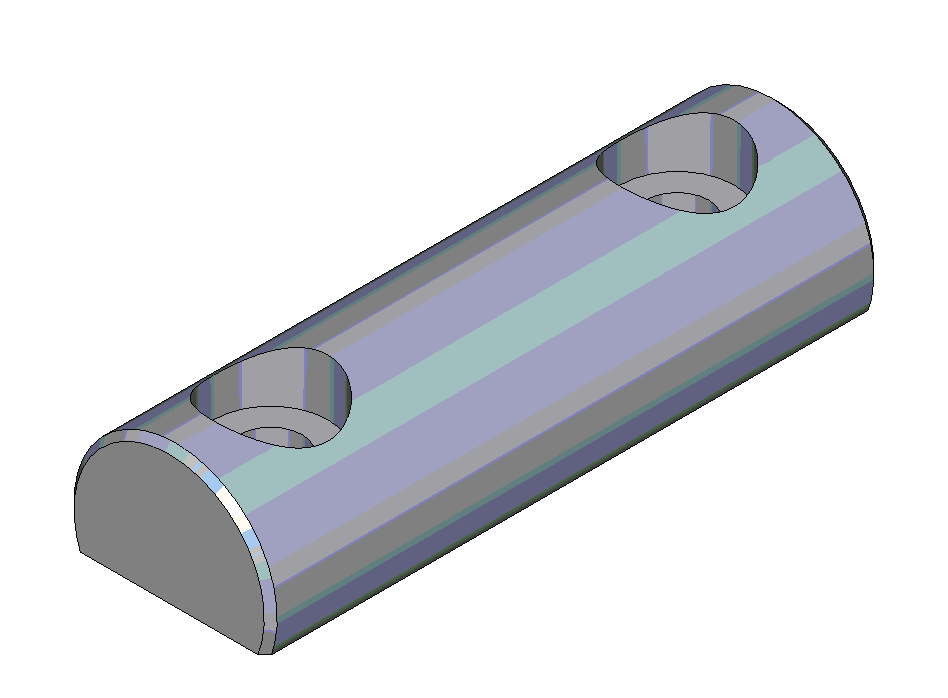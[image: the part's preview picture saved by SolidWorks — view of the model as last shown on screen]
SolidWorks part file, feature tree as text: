
SOLIDWORKS PART (.sldprt)
format: sldprt  version: not decoded by parser v0  size: 414,208 bytes
history: native  units: mm
features: sketch x5, plane x4, cut_extrude x3, material x1, extrude x1, chamfer x1, cut_revolve x1, mirror x1 + 3 further entries (+11 scaffold rows collapsed; 1 parser-record rows omitted)
feature tree (32):
  scaffold x11  (default folders/planes/origin — collapsed)
  material  "Stainless Steel 440C 58Rc"
  plane  "Plane X-Y"
  plane  "Plane X-Z"
  plane  "Plane Y-Z"
  "Design Table"
  "Axis - Y"
  "Axis - Z"
  sketch  "Sketch1"  dims[Cylinder_dia=12.7mm]
  extrude  "Extrude1"  Depth=38.1mm
  chamfer  "Chamfer1"  Distance=0.4064mm Angle=45deg
  sketch  "Sketch2"  dims[Truncated_height=8.4836mm D1=~11.961647mm]
  cut_extrude  "Truncated"  [1 undecoded]
  sketch  "Sketch3"  dims[D3=0.508mm Recess_width=8.4836mm Recess_length=34.925mm D4=3.175mm D5=1.5875mm D1=1.5875mm]
  cut_extrude  "Recessed"  Depth=0.127mm
  sketch  "Sketch5"  dims[D1=12.7mm Thru_hole_dia=3.9116mm Ct_bore_dia=7.1374mm Ct_bore_depth=3.5052mm]
  parser-record x1  (decoder bookkeeping rows leaked as tree rows — omitted from the tree; the rows remain in map.json)
  cut_revolve  "CtBored Hole Cut-Revolve1"  Angle=360deg
  mirror  "CtBored Hole Mirror1"
  plane  "Bottom Plane"
  sketch  "Sketch6"  dims[D1=~3.96875mm D2=25.4mm]
  cut_extrude  "Blind Holes"  Depth=6.35mm
decode coverage: 10 of 12 modeling features carry decoded parameters; 3 rows unclassified (native names shown)
note: ~ marks probable driven/reference dimensions
note: 1 parameter value undecoded
note: suppression state not decoded; provenance and decode notes live in map.json
